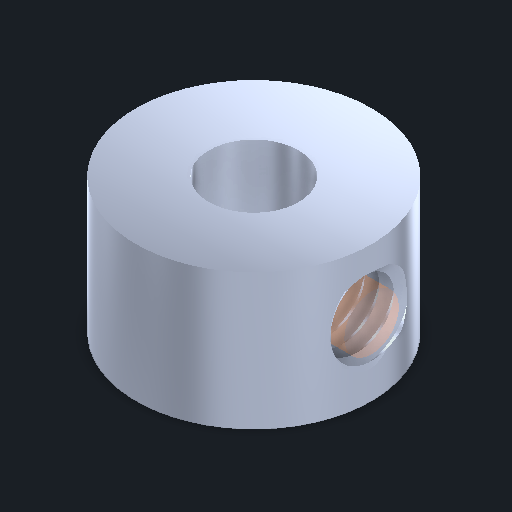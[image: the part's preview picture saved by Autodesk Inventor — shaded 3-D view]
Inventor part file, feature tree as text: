
AUTODESK INVENTOR PART (.ipt)
format: ipt  version: 2024 (Build 280153000, 153)  size: 614,400 bytes
history: native  units: in
note: dims shown in document units (in); Inventor stores cm internally (conversion verified against a paired STEP export)
features: extrude x3, other x2, sketch x2, imported_body x1, plane x1
ambient origin geometry x8: Origin, YZ Plane, XZ Plane, XY Plane, X Axis, Y Axis, Z Axis, Center Point
bodies: Body1 (feature_tree), Body2 (feature_tree)
feature tree (9):
  parser-record x1  (decoder bookkeeping rows leaked as tree rows — omitted from the tree; the rows remain in map.json)
  imported_body  "Base1"
  extrude  "Extrusion1"  Depth=0.005in TaperAngle=0.0deg
  extrude  "Extrusion2"  Depth=1.0in TaperAngle=0.0deg
  plane  "Work Plane1"
  sketch  "Sketch1"  dims[d3=0.005in d4=0.0in d5=0.005in d6=0.0in]
  sketch  "Sketch2"  dims[d7=0.1in d8=1.0in d9=0.0in]
  other  "Srf1"
  extrude  "ExtrusionSrf1"  [1 undecoded]
note: 1 required parameter value undecoded (feature->parameter linkage not recoverable at this tier; creation-order binding heuristic only, values carry confidence <= 0.55)
